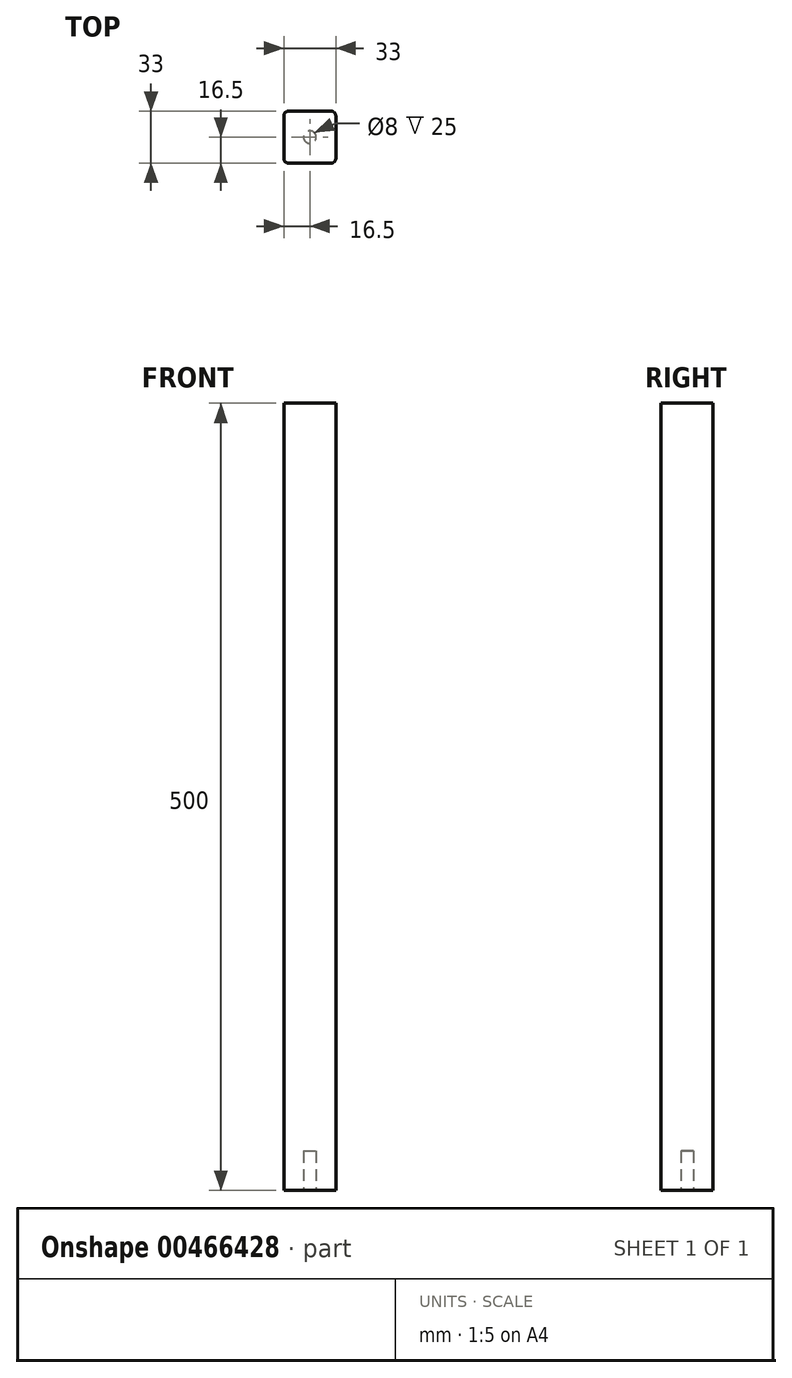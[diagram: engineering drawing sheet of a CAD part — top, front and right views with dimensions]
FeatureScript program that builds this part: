
annotation { "Feature Type Name" : "Feature", "Feature Type Description" : "" }
export const myFeature = defineFeature(function(context is Context, id is Id, definition is map)
    precondition{}
    {
        {
            var Q0;
            Q0=qCreatedBy(makeId("Top.planeOp"),FACE);
            var sketch = newSketch(context, id + "F0", { "sketchPlane" : qUnion([Q0])});
            skLineSegment(sketch, "E0.bottom", {"start": v(0, 0) * mm, "end": v(33, 0) * mm});
            skLineSegment(sketch, "E0.top", {"start": v(0, -33) * mm, "end": v(33, -33) * mm});
            skLineSegment(sketch, "E0.left", {"start": v(0, 0) * mm, "end": v(0, -33) * mm});
            skLineSegment(sketch, "E0.right", {"start": v(33, 0) * mm, "end": v(33, -33) * mm});
            skSolve(sketch);
        }
        {
            var Q0;
            Q0=makeQuery(id+"F0.imprint","IMPRINT",FACE,{"disambiguationData":[TD([[makeQuery(id+"F0.imprint","IMPRINT",EDGE,{"derivedFrom":sQuery(id+"F0.wireOp",EDGE,"E0.bottom")}),-1.0]])]});
            extrude(context, id + "F1", {"entities" : qUnion([Q0]), "depth" : 500 * mm});
        }
        {
            var Q0;
            Q0=makeQuery(id+"F1.opExtrude","SWEPT_EDGE",EDGE,{"disambiguationData":[OSD([sQuery(id+"F0.wireOp",EDGE,"E0.bottom"),sQuery(id+"F0.wireOp",EDGE,"E0.right")])]});
            var Q1;
            Q1=makeQuery(id+"F1.opExtrude","SWEPT_EDGE",EDGE,{"disambiguationData":[OSD([sQuery(id+"F0.wireOp",EDGE,"E0.top"),sQuery(id+"F0.wireOp",EDGE,"E0.right")])]});
            var Q2;
            Q2=makeQuery(id+"F1.opExtrude","SWEPT_EDGE",EDGE,{"disambiguationData":[OSD([sQuery(id+"F0.wireOp",EDGE,"E0.top"),sQuery(id+"F0.wireOp",EDGE,"E0.left")])]});
            var Q3;
            Q3=makeQuery(id+"F1.opExtrude","SWEPT_EDGE",EDGE,{"disambiguationData":[OSD([sQuery(id+"F0.wireOp",EDGE,"E0.bottom"),sQuery(id+"F0.wireOp",EDGE,"E0.left")])]});
            fillet(context, id + "F2", {"entities" : qUnion([Q0, Q1, Q2, Q3]), "radius" : 3 * mm, "tangentPropagation" : true, "allowEdgeOverflow" : false});
        }
        {
            var Q0;
            Q0=makeQuery(id+"F1.opExtrude","CAP_FACE",FACE,{"disambiguationData":[OSD([sQuery(id+"F0.wireOp",EDGE,"E0.bottom"),sQuery(id+"F0.wireOp",EDGE,"E0.top"),sQuery(id+"F0.wireOp",EDGE,"E0.left"),sQuery(id+"F0.wireOp",EDGE,"E0.right")])],"isStart":true});
            var sketch = newSketch(context, id + "F3", { "sketchPlane" : qUnion([Q0])});
            skCircle(sketch, "E1", {"center": v(16.5, 16.5) * mm, "radius": 4 * mm});
            skPoint(sketch, "E1.centerSnap0", {"position": v(16.5, 33) * mm});
            skPoint(sketch, "E1.centerSnap1", {"position": v(33, 16.5) * mm});
            skSolve(sketch);
        }
        {
            var Q0;
            Q0=makeQuery(id+"F3.imprint","IMPRINT",FACE,{"disambiguationData":[TD([[makeQuery(id+"F3.imprint","IMPRINT",EDGE,{"derivedFrom":sQuery(id+"F3.wireOp",EDGE,"E1")}),1.0]])]});
            extrude(context, id + "F4", {"entities" : qUnion([Q0]), "operationType" : NewBodyOperationType.REMOVE, "oppositeDirection" : true, "depth" : 25 * mm});
        }
    });
